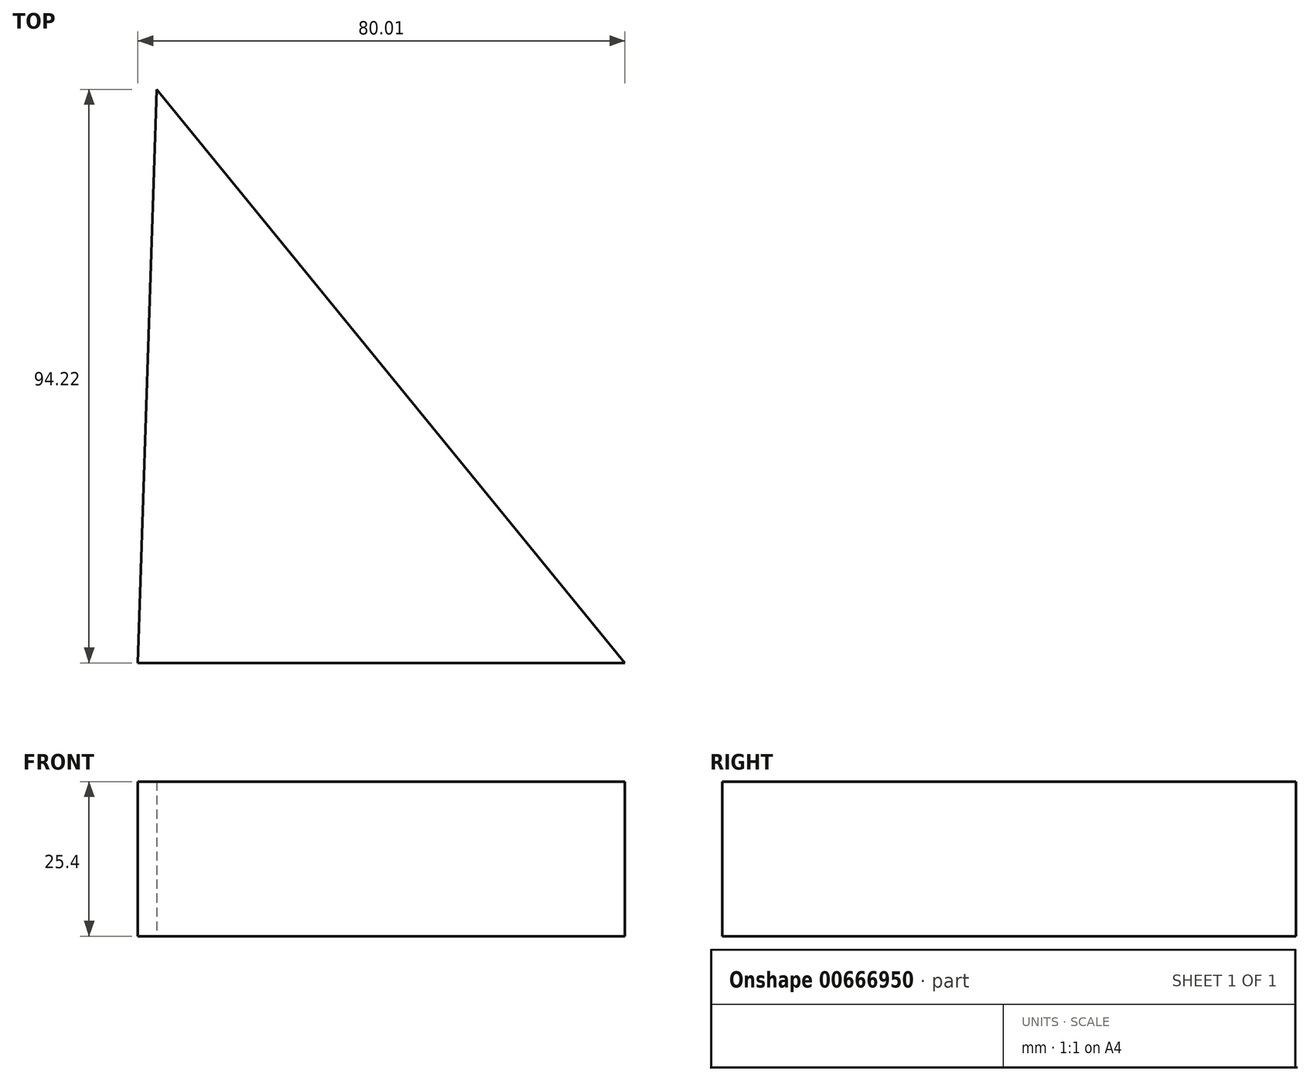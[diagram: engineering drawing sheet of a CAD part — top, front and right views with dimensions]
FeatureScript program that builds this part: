
annotation { "Feature Type Name" : "Feature", "Feature Type Description" : "" }
export const myFeature = defineFeature(function(context is Context, id is Id, definition is map)
    precondition{}
    {
        {
            var Q0;
            Q0=qCreatedBy(makeId("Top.planeOp"),FACE);
            var sketch = newSketch(context, id + "F0", { "sketchPlane" : qUnion([Q0])});
            skLineSegment(sketch, "E0", {"start": v(-53.76, -27.48) * mm, "end": v(26.25, -27.48) * mm});
            skLineSegment(sketch, "E1", {"start": v(26.25, -27.48) * mm, "end": v(-50.68, 66.74) * mm});
            skLineSegment(sketch, "E2", {"start": v(-50.68, 66.74) * mm, "end": v(-53.76, -27.48) * mm});
            skSolve(sketch);
        }
        {
            var Q0;
            Q0 = qSketchRegion(id + "F0", true);
            extrude(context, id + "F1", {"entities" : qUnion([Q0]), "depth" : 25.4 * mm, "offsetDistance" : 25.4 * mm});
        }
    });
